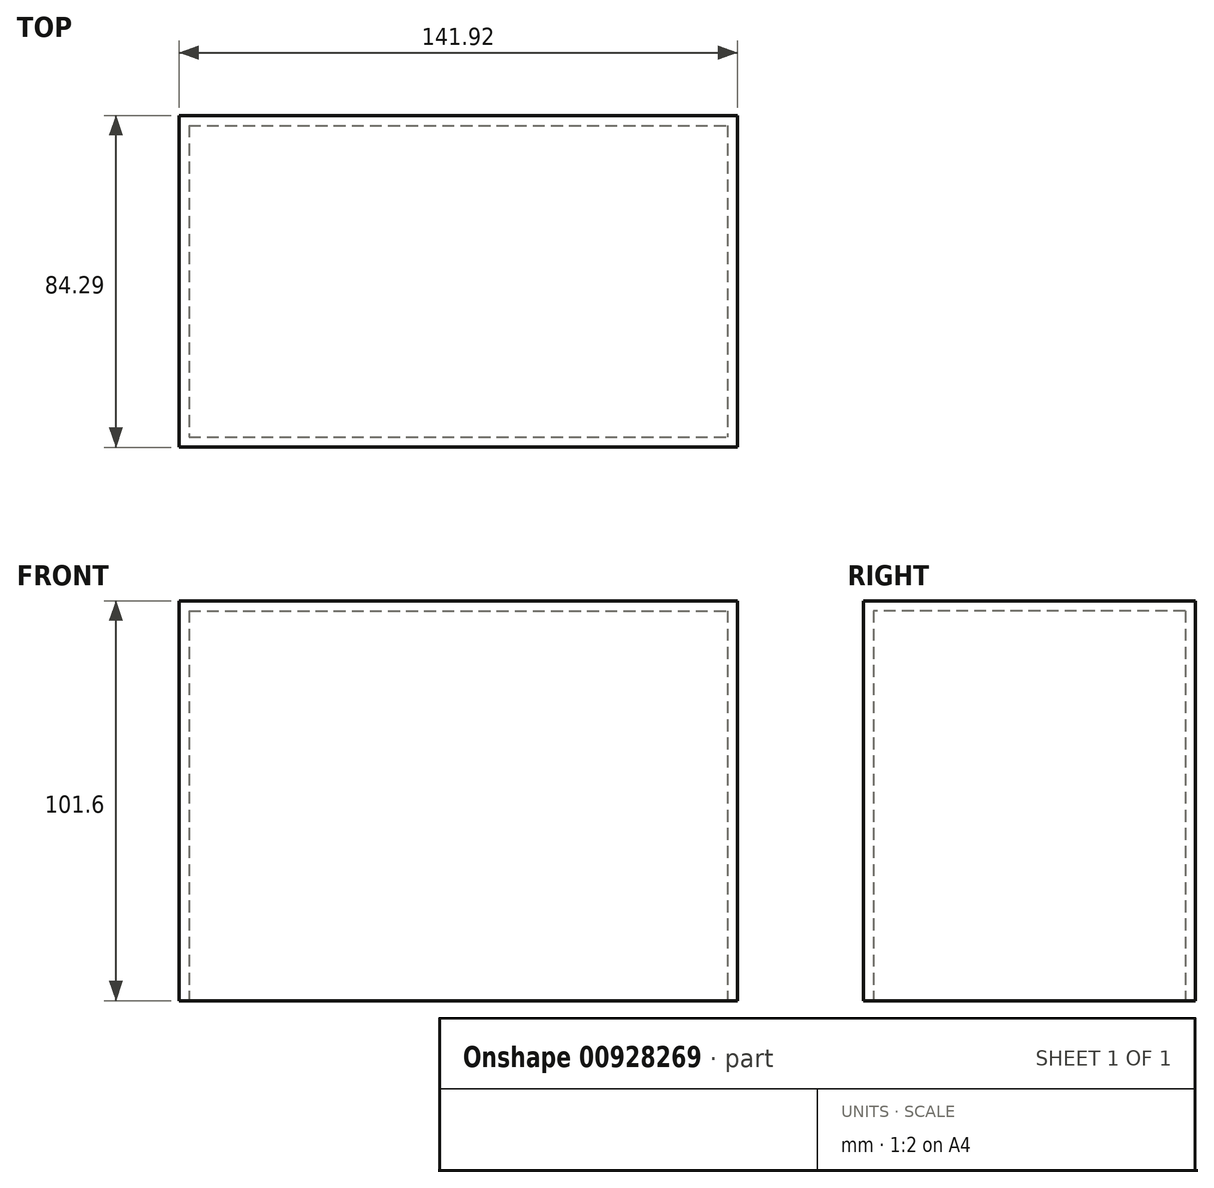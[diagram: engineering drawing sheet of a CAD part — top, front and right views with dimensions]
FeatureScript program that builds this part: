
annotation { "Feature Type Name" : "Feature", "Feature Type Description" : "" }
export const myFeature = defineFeature(function(context is Context, id is Id, definition is map)
    precondition{}
    {
        {
            var Q0;
            Q0=qCreatedBy(makeId("Top.planeOp"),FACE);
            var sketch = newSketch(context, id + "F0", { "sketchPlane" : qUnion([Q0])});
            skLineSegment(sketch, "E0.bottom", {"start": v(-74.53, 0) * mm, "end": v(67.4, 0) * mm});
            skLineSegment(sketch, "E0.top", {"start": v(-74.53, -84.29) * mm, "end": v(67.4, -84.29) * mm});
            skLineSegment(sketch, "E0.left", {"start": v(-74.53, 0) * mm, "end": v(-74.53, -84.29) * mm});
            skLineSegment(sketch, "E0.right", {"start": v(67.4, 0) * mm, "end": v(67.4, -84.29) * mm});
            skSolve(sketch);
        }
        {
            var Q0;
            Q0=makeQuery(id+"F0.imprint","IMPRINT",FACE,{"disambiguationData":[TD([[makeQuery(id+"F0.imprint","IMPRINT",EDGE,{"derivedFrom":sQuery(id+"F0.wireOp",EDGE,"E0.bottom")}),-1.0]])]});
            extrude(context, id + "F1", {"entities" : qUnion([Q0]), "depth" : 101.6 * mm, "offsetDistance" : 25.4 * mm});
        }
        {
            var Q0;
            Q0=makeQuery(id+"F1.opExtrude","CAP_FACE",FACE,{"disambiguationData":[OSD([sQuery(id+"F0.wireOp",EDGE,"E0.bottom"),sQuery(id+"F0.wireOp",EDGE,"E0.top"),sQuery(id+"F0.wireOp",EDGE,"E0.left"),sQuery(id+"F0.wireOp",EDGE,"E0.right")])],"isStart":true});
            shell(context, id + "F2", {"entities" : qUnion([Q0]), "thickness" : 2.54 * mm});
        }
        {
            var Q0;
            Q0=makeQuery(id+"F2.opShell","OFFSET_FACE",FACE,{"disambiguationData":[OSD([sQuery(id+"F0.wireOp",EDGE,"E0.top")])]});
            var sketch = newSketch(context, id + "F3", { "sketchPlane" : qUnion([Q0])});
            skLineSegment(sketch, "E1.bottom", {"start": v(-64.85, 0) * mm, "end": v(56.57, 0) * mm});
            skLineSegment(sketch, "E1.top", {"start": v(-64.85, -1305.93) * mm, "end": v(56.57, -1305.93) * mm});
            skLineSegment(sketch, "E1.left", {"start": v(-64.85, 0) * mm, "end": v(-64.85, -1305.93) * mm});
            skLineSegment(sketch, "E1.right", {"start": v(56.57, 0) * mm, "end": v(56.57, -1305.93) * mm});
            skSolve(sketch);
        }
    });
